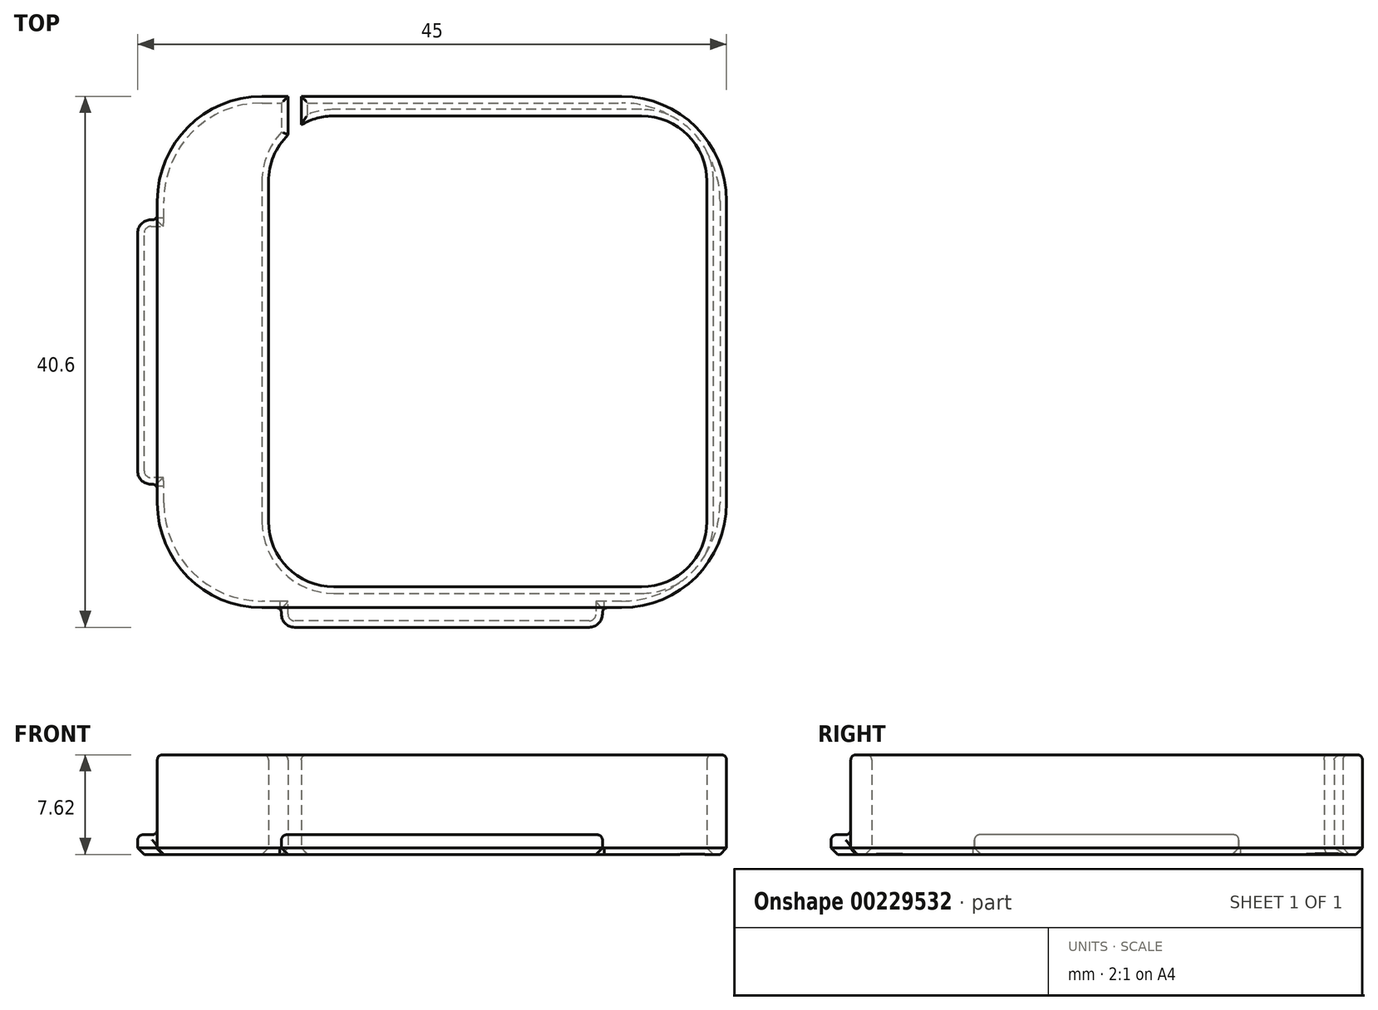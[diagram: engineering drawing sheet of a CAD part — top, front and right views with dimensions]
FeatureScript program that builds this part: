
annotation { "Feature Type Name" : "Feature", "Feature Type Description" : "" }
export const myFeature = defineFeature(function(context is Context, id is Id, definition is map)
    precondition{}
    {
        {
            var Q0;
            Q0=qCreatedBy(makeId("Top.planeOp"),FACE);
            var sketch = newSketch(context, id + "F0", { "sketchPlane" : qUnion([Q0])});
            skLineSegment(sketch, "E0.bottom", {"start": v(-14.69, 21.76) * mm, "end": v(-13.19, 21.76) * mm});
            skLineSegment(sketch, "E0.top", {"start": v(-14.69, -17.34) * mm, "end": v(12.81, -17.34) * mm});
            skLineSegment(sketch, "E0.left", {"start": v(-22.69, 13.76) * mm, "end": v(-22.69, -9.34) * mm});
            skLineSegment(sketch, "E0.right", {"start": v(20.81, 13.76) * mm, "end": v(20.81, -9.34) * mm});
            skLineSegment(sketch, "E1.bottom", {"start": v(14.31, 20.26) * mm, "end": v(-9.19, 20.26) * mm});
            skLineSegment(sketch, "E1.top", {"start": v(14.31, -15.74) * mm, "end": v(-9.19, -15.74) * mm});
            skLineSegment(sketch, "E1.left", {"start": v(19.31, 15.26) * mm, "end": v(19.31, -10.74) * mm});
            skLineSegment(sketch, "E1.right", {"start": v(-14.19, 15.26) * mm, "end": v(-14.19, -10.74) * mm});
            skPoint(sketch, "E2.visualSharp", {"position": v(-14.19, 20.26) * mm});
            skArc(sketch, "E2.filletArc", {"start": v(-9.19, 20.26) * mm, "mid": v(-10.48, 20.09) * mm, "end": v(-11.69, 19.59) * mm});
            skPoint(sketch, "E3.visualSharp", {"position": v(-14.19, -15.74) * mm});
            skArc(sketch, "E3.filletArc", {"start": v(-14.19, -10.74) * mm, "mid": v(-12.72, -14.28) * mm, "end": v(-9.19, -15.74) * mm});
            skPoint(sketch, "E4.visualSharp", {"position": v(19.31, -15.74) * mm});
            skArc(sketch, "E4.filletArc", {"start": v(14.31, -15.74) * mm, "mid": v(17.85, -14.28) * mm, "end": v(19.31, -10.74) * mm});
            skPoint(sketch, "E5.visualSharp", {"position": v(19.31, 20.26) * mm});
            skArc(sketch, "E5.filletArc", {"start": v(19.31, 15.26) * mm, "mid": v(17.85, 18.8) * mm, "end": v(14.31, 20.26) * mm});
            skPoint(sketch, "E6.visualSharp", {"position": v(-22.69, -17.34) * mm});
            skArc(sketch, "E6.filletArc", {"start": v(-22.69, -9.34) * mm, "mid": v(-20.35, -15) * mm, "end": v(-14.69, -17.34) * mm});
            skPoint(sketch, "E7.visualSharp", {"position": v(-22.69, 21.76) * mm});
            skArc(sketch, "E7.filletArc", {"start": v(-14.69, 21.76) * mm, "mid": v(-20.35, 19.41) * mm, "end": v(-22.69, 13.76) * mm});
            skPoint(sketch, "E8.visualSharp", {"position": v(20.81, 21.76) * mm});
            skArc(sketch, "E8.filletArc", {"start": v(20.81, 13.76) * mm, "mid": v(18.47, 19.41) * mm, "end": v(12.81, 21.76) * mm});
            skPoint(sketch, "E9.visualSharp", {"position": v(20.81, -17.34) * mm});
            skArc(sketch, "E9.filletArc", {"start": v(12.81, -17.34) * mm, "mid": v(18.47, -15) * mm, "end": v(20.81, -9.34) * mm});
            skLineSegment(sketch, "E10", {"start": v(-12.69, 21.76) * mm, "end": v(-12.69, 18.83) * mm});
            skLineSegment(sketch, "E11", {"start": v(-11.69, 19.59) * mm, "end": v(-11.69, 21.76) * mm});
            skArc(sketch, "E12", {"start": v(-12.69, 18.83) * mm, "mid": v(-13.8, 17.2) * mm, "end": v(-14.19, 15.26) * mm});
            skLineSegment(sketch, "E13", {"start": v(-11.69, 21.76) * mm, "end": v(12.81, 21.76) * mm});
            skLineSegment(sketch, "E14", {"start": v(-13.19, 21.76) * mm, "end": v(-12.69, 21.76) * mm});
            skSolve(sketch);
        }
        {
            var Q0;
            Q0 = qSketchRegion(id + "F0", true);
            extrude(context, id + "F1", {"entities" : qUnion([Q0]), "depth" : 7.62 * mm});
        }
        {
            var Q0;
            Q0=qCreatedBy(makeId("Top.planeOp"),FACE);
            var sketch = newSketch(context, id + "F2", { "sketchPlane" : qUnion([Q0])});
            skLineSegment(sketch, "E15.0", {"start": v(-22.69, 13.76) * mm, "end": v(-22.69, -9.34) * mm});
            skLineSegment(sketch, "E15.1", {"start": v(-14.69, -17.34) * mm, "end": v(12.81, -17.34) * mm});
            skLineSegment(sketch, "E16.bottom", {"start": v(-22.69, 12.31) * mm, "end": v(-23.19, 12.31) * mm});
            skLineSegment(sketch, "E16.top", {"start": v(-22.69, -7.9) * mm, "end": v(-23.19, -7.9) * mm});
            skLineSegment(sketch, "E16.left", {"start": v(-22.69, 12.31) * mm, "end": v(-22.69, -7.9) * mm});
            skLineSegment(sketch, "E16.right", {"start": v(-24.19, 11.31) * mm, "end": v(-24.19, -6.9) * mm});
            skPoint(sketch, "E17", {"position": v(-24.19, 2.2) * mm});
            skPoint(sketch, "E18.visualSharp", {"position": v(-24.19, 12.31) * mm});
            skArc(sketch, "E18.filletArc", {"start": v(-23.19, 12.31) * mm, "mid": v(-23.9, 12.02) * mm, "end": v(-24.19, 11.31) * mm});
            skPoint(sketch, "E19.visualSharp", {"position": v(-24.19, -7.9) * mm});
            skArc(sketch, "E19.filletArc", {"start": v(-24.19, -6.9) * mm, "mid": v(-23.9, -7.6) * mm, "end": v(-23.19, -7.9) * mm});
            skPoint(sketch, "E20", {"position": v(-22.69, 2.2) * mm});
            skLineSegment(sketch, "E21.bottom", {"start": v(-13.2, -17.34) * mm, "end": v(11.33, -17.34) * mm});
            skLineSegment(sketch, "E21.top", {"start": v(-12.2, -18.84) * mm, "end": v(10.33, -18.84) * mm});
            skLineSegment(sketch, "E21.left", {"start": v(-13.2, -17.34) * mm, "end": v(-13.2, -17.84) * mm});
            skLineSegment(sketch, "E21.right", {"start": v(11.33, -17.34) * mm, "end": v(11.33, -17.84) * mm});
            skPoint(sketch, "E22", {"position": v(-0.94, -17.34) * mm});
            skPoint(sketch, "E23", {"position": v(-0.94, -18.84) * mm});
            skPoint(sketch, "E24.visualSharp", {"position": v(-13.2, -18.84) * mm});
            skArc(sketch, "E24.filletArc", {"start": v(-13.2, -17.84) * mm, "mid": v(-12.91, -18.55) * mm, "end": v(-12.2, -18.84) * mm});
            skPoint(sketch, "E25.visualSharp", {"position": v(11.33, -18.84) * mm});
            skArc(sketch, "E25.filletArc", {"start": v(10.33, -18.84) * mm, "mid": v(11.03, -18.55) * mm, "end": v(11.33, -17.84) * mm});
            skSolve(sketch);
        }
        {
            var Q0;
            Q0 = qSketchRegion(id + "F2", true);
            extrude(context, id + "F3", {"entities" : qUnion([Q0]), "operationType" : NewBodyOperationType.ADD, "depth" : 1.5 * mm});
        }
        {
            var Q0;
            Q0=makeQuery(id+"F1.opExtrude","CAP_FACE",FACE,{"disambiguationData":[OSD([sQuery(id+"F0.wireOp",EDGE,"E0.bottom"),sQuery(id+"F0.wireOp",EDGE,"E0.top"),sQuery(id+"F0.wireOp",EDGE,"E0.left"),sQuery(id+"F0.wireOp",EDGE,"E0.right"),sQuery(id+"F0.wireOp",EDGE,"E1.bottom"),sQuery(id+"F0.wireOp",EDGE,"E1.top"),sQuery(id+"F0.wireOp",EDGE,"E1.left"),sQuery(id+"F0.wireOp",EDGE,"E1.right"),sQuery(id+"F0.wireOp",EDGE,"E2.filletArc"),sQuery(id+"F0.wireOp",EDGE,"E3.filletArc"),sQuery(id+"F0.wireOp",EDGE,"E4.filletArc"),sQuery(id+"F0.wireOp",EDGE,"E5.filletArc"),sQuery(id+"F0.wireOp",EDGE,"E6.filletArc"),sQuery(id+"F0.wireOp",EDGE,"E7.filletArc"),sQuery(id+"F0.wireOp",EDGE,"E8.filletArc"),sQuery(id+"F0.wireOp",EDGE,"E9.filletArc"),sQuery(id+"F0.wireOp",EDGE,"E10"),sQuery(id+"F0.wireOp",EDGE,"E11"),sQuery(id+"F0.wireOp",EDGE,"E12"),sQuery(id+"F0.wireOp",EDGE,"E13")])],"isStart":false});
            var Q1;
            Q1=makeQuery(id+"F3.opExtrude","CAP_FACE",FACE,{"disambiguationData":[OSD([sQuery(id+"F2.wireOp",EDGE,"E21.bottom"),sQuery(id+"F2.wireOp",EDGE,"E21.top"),sQuery(id+"F2.wireOp",EDGE,"E21.left"),sQuery(id+"F2.wireOp",EDGE,"E21.right"),sQuery(id+"F2.wireOp",EDGE,"E24.filletArc"),sQuery(id+"F2.wireOp",EDGE,"E25.filletArc")])],"isStart":false});
            var Q2;
            Q2=makeQuery(id+"F3.opExtrude","CAP_FACE",FACE,{"disambiguationData":[OSD([sQuery(id+"F2.wireOp",EDGE,"E16.bottom"),sQuery(id+"F2.wireOp",EDGE,"E16.top"),sQuery(id+"F2.wireOp",EDGE,"E16.left"),sQuery(id+"F2.wireOp",EDGE,"E16.right"),sQuery(id+"F2.wireOp",EDGE,"E18.filletArc"),sQuery(id+"F2.wireOp",EDGE,"E19.filletArc")])],"isStart":false});
            fillet(context, id + "F4", {"entities" : qUnion([Q0, Q1, Q2]), "radius" : 0.4 * mm, "tangentPropagation" : true, "allowEdgeOverflow" : false});
        }
        {
            var Q0;
            Q0=makeQuery(id+"F3.boolean.opBoolean","MERGE",FACE,{"derivedFrom":[makeQuery(id+"F1.opExtrude","CAP_FACE",FACE,{"disambiguationData":[OSD([sQuery(id+"F0.wireOp",EDGE,"E0.bottom"),sQuery(id+"F0.wireOp",EDGE,"E0.top"),sQuery(id+"F0.wireOp",EDGE,"E0.left"),sQuery(id+"F0.wireOp",EDGE,"E0.right"),sQuery(id+"F0.wireOp",EDGE,"E1.bottom"),sQuery(id+"F0.wireOp",EDGE,"E1.top"),sQuery(id+"F0.wireOp",EDGE,"E1.left"),sQuery(id+"F0.wireOp",EDGE,"E1.right"),sQuery(id+"F0.wireOp",EDGE,"E2.filletArc"),sQuery(id+"F0.wireOp",EDGE,"E3.filletArc"),sQuery(id+"F0.wireOp",EDGE,"E4.filletArc"),sQuery(id+"F0.wireOp",EDGE,"E5.filletArc"),sQuery(id+"F0.wireOp",EDGE,"E6.filletArc"),sQuery(id+"F0.wireOp",EDGE,"E7.filletArc"),sQuery(id+"F0.wireOp",EDGE,"E8.filletArc"),sQuery(id+"F0.wireOp",EDGE,"E9.filletArc"),sQuery(id+"F0.wireOp",EDGE,"E10"),sQuery(id+"F0.wireOp",EDGE,"E11"),sQuery(id+"F0.wireOp",EDGE,"E12"),sQuery(id+"F0.wireOp",EDGE,"E13"),sQuery(id+"F0.wireOp",EDGE,"E14")])],"isStart":true}),makeQuery(id+"F3.opExtrude","CAP_FACE",FACE,{"disambiguationData":[OSD([sQuery(id+"F2.wireOp",EDGE,"E16.bottom"),sQuery(id+"F2.wireOp",EDGE,"E16.top"),sQuery(id+"F2.wireOp",EDGE,"E16.left"),sQuery(id+"F2.wireOp",EDGE,"E16.right"),sQuery(id+"F2.wireOp",EDGE,"E18.filletArc"),sQuery(id+"F2.wireOp",EDGE,"E19.filletArc")])],"isStart":true}),makeQuery(id+"F3.opExtrude","CAP_FACE",FACE,{"disambiguationData":[OSD([sQuery(id+"F2.wireOp",EDGE,"E21.bottom"),sQuery(id+"F2.wireOp",EDGE,"E21.top"),sQuery(id+"F2.wireOp",EDGE,"E21.left"),sQuery(id+"F2.wireOp",EDGE,"E21.right"),sQuery(id+"F2.wireOp",EDGE,"E24.filletArc"),sQuery(id+"F2.wireOp",EDGE,"E25.filletArc")])],"isStart":true})]});
            chamfer(context, id + "F5", {"entities" : qUnion([Q0]), "width" : .5 * mm, "tangentPropagation" : true});
        }
    });
